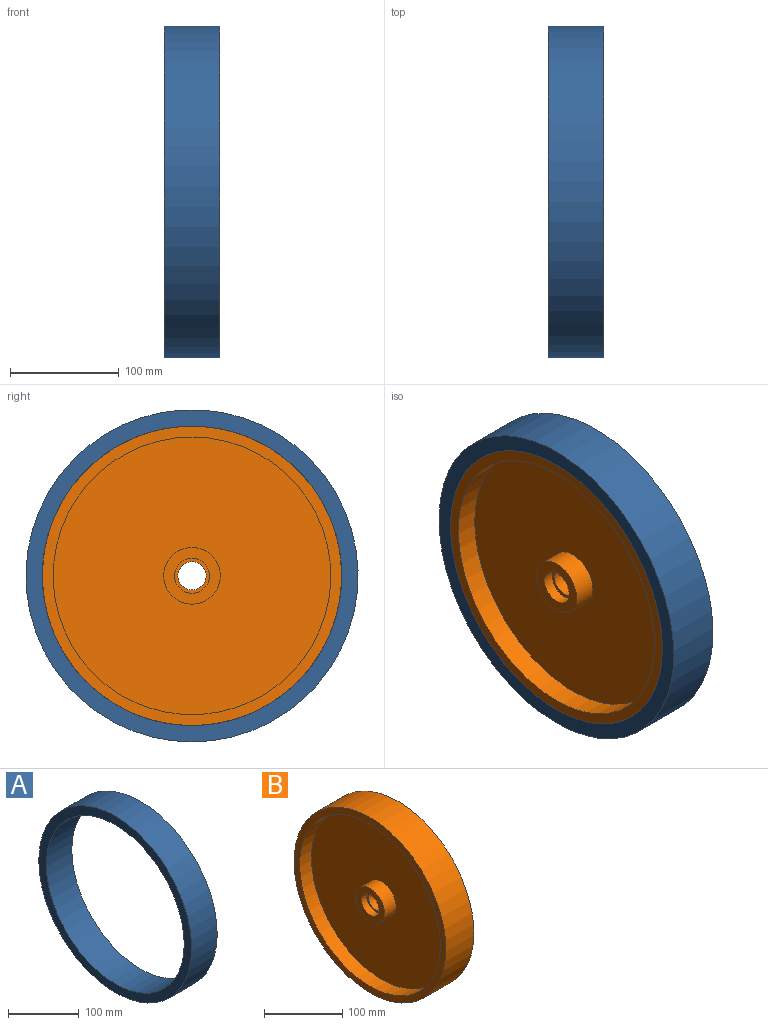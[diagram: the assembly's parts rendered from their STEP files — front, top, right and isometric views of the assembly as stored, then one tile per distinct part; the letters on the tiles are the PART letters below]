
ASSEMBLY  parts=2 mates=1
PART A: 4 faces, bbox 50.8x304.8x304.8 mm
  f0: plane 304.8x304.8mm, normal (-1,0,0), area 13656.5mm2, adj f1,f3
  f1: cylinder r=137.4mm len=274.8mm, axis (-1,0,0), area 43856.1mm2, adj f0,f2
  f2: plane 304.8x304.8mm, normal (1,0,0), area 13656.5mm2, adj f1,f3
  f3: cylinder r=152.4mm len=304.8mm, axis (-1,0,0), area 48643.9mm2, adj f0,f2
PART B: 16 faces, bbox 50.8x274.8x274.8 mm
  f0: cylinder r=137.4mm len=274.8mm, axis (-1,0,0), area 43856.1mm2, adj f1,f15
  f1: plane 274.8x274.8mm, normal (-1,0,0), area 8318.9mm2, adj f0,f2
  f2: cylinder r=127.4mm len=254.8mm, axis (-1,0,0), area 17130.2mm2, adj f1,f3
  f3: plane 254.8x254.8mm, normal (-1,0,0), area 48866.7mm2, adj f2,f4
  f4: cylinder r=26mm len=52mm, axis (-1,0,0), area 3430.6mm2, adj f3,f5
  f5: plane 52x52mm, normal (-1,0,0), area 1319.5mm2, adj f4,f6
  f6: cylinder r=16mm len=32mm, axis (-1,0,0), area 1005.3mm2, adj f5,f7
  f7: plane 32x32mm, normal (-1,0,0), area 273.3mm2, adj f6,f8
  f8: cylinder r=13mm len=30mm, axis (-1,0,0), area 2450.4mm2, adj f7,f9
  f9: plane 32x32mm, normal (1,0,0), area 273.3mm2, adj f8,f10
  f10: cylinder r=16mm len=32mm, axis (-1,0,0), area 1005.3mm2, adj f9,f11
  f11: plane 52x52mm, normal (1,0,0), area 1319.5mm2, adj f10,f12
  f12: cylinder r=26mm len=52mm, axis (-1,0,0), area 3430.6mm2, adj f11,f13
  f13: plane 254.8x254.8mm, normal (1,0,0), area 48866.7mm2, adj f12,f14
  f14: cylinder r=127.4mm len=254.8mm, axis (-1,0,0), area 17130.2mm2, adj f13,f15
  f15: plane 274.8x274.8mm, normal (1,0,0), area 8318.9mm2, adj f0,f14
PLACE A rot(axis=(0,1,0),180deg) t=(-15,0,0)mm
PLACE B rot(axis=(0,0,1),180deg) t=(-15,0,0)mm
MATE fastened A.f1 <-> B.f0  axis (1,0,0) through (-15,0,0)mm
